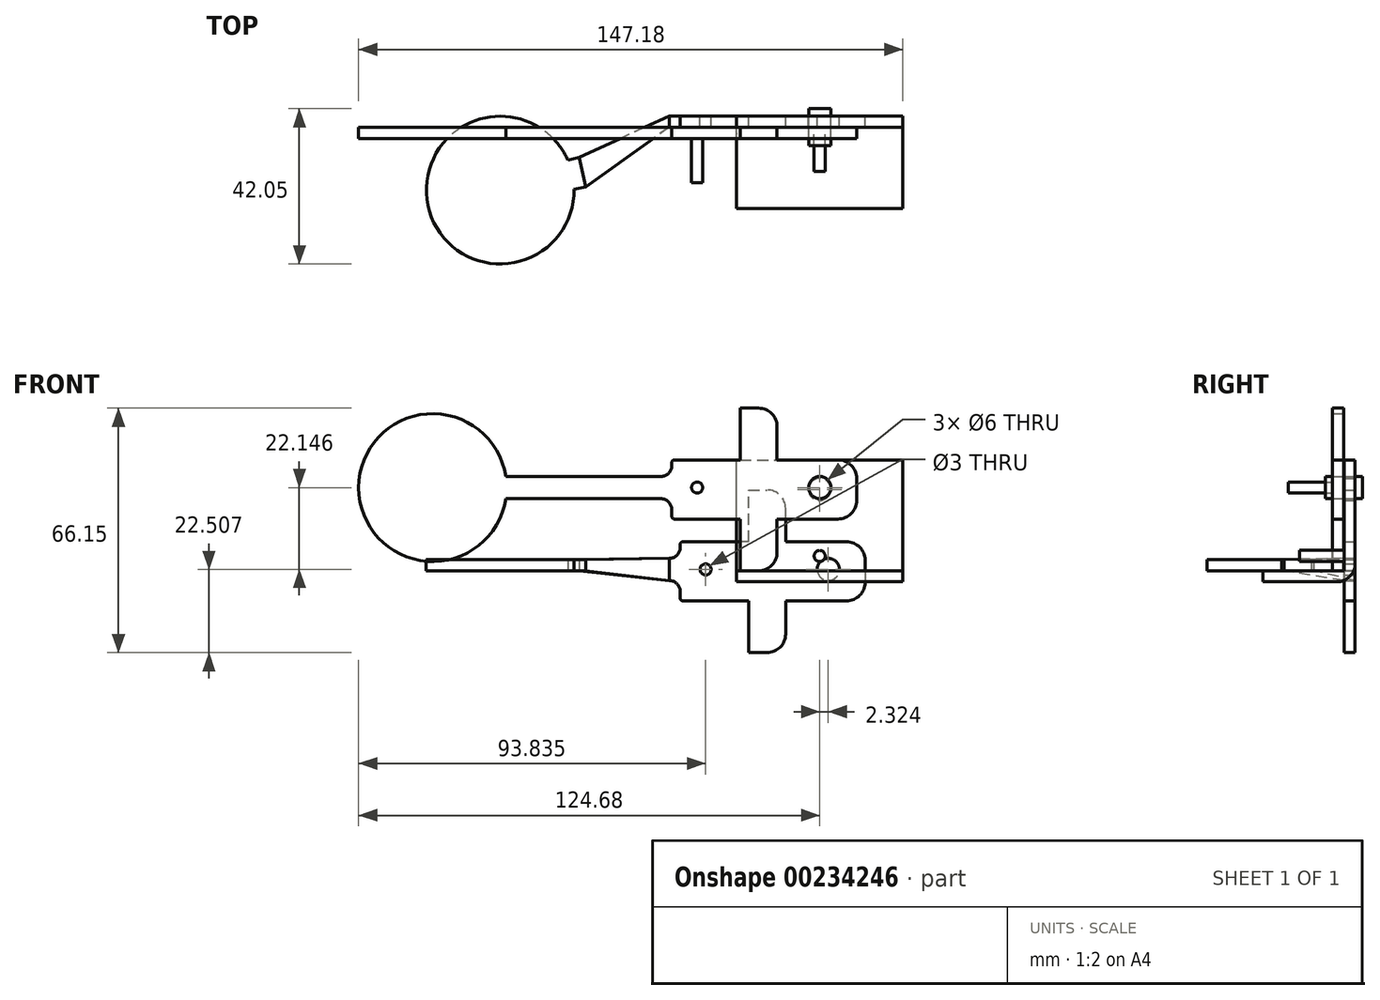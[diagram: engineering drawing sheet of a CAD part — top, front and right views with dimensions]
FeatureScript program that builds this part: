
annotation { "Feature Type Name" : "Feature", "Feature Type Description" : "" }
export const myFeature = defineFeature(function(context is Context, id is Id, definition is map)
    precondition{}
    {
        {
            var Q0;
            Q0=qCreatedBy(makeId("Front.planeOp"),FACE);
            var sketch = newSketch(context, id + "F0", { "sketchPlane" : qUnion([Q0])});
            skLineSegment(sketch, "E0.bottom", {"start": v(0, 0) * mm, "end": v(45, 0) * mm});
            skLineSegment(sketch, "E0.top", {"start": v(0, 30) * mm, "end": v(45, 30) * mm});
            skLineSegment(sketch, "E0.left", {"start": v(0, 0) * mm, "end": v(0, 30) * mm});
            skLineSegment(sketch, "E0.right", {"start": v(45, 0) * mm, "end": v(45, 30) * mm});
            skLineSegment(sketch, "E1.top", {"start": v(0, -3) * mm, "end": v(45, -3) * mm});
            skLineSegment(sketch, "E1.left", {"start": v(0, 0) * mm, "end": v(0, -3) * mm});
            skLineSegment(sketch, "E1.right", {"start": v(45, 0) * mm, "end": v(45, -3) * mm});
            skPoint(sketch, "E2", {"position": v(22.5, 22) * mm});
            skCircle(sketch, "E3", {"center": v(22.5, 4) * mm, "radius": 1.5 * mm});
            skSolve(sketch);
        }
        {
            var Q0;
            Q0=makeQuery(id+"F0.imprint","IMPRINT",FACE,{"disambiguationData":[TD([[makeQuery(id+"F0.imprint","IMPRINT",EDGE,{"derivedFrom":sQuery(id+"F0.wireOp",EDGE,"E0.top")}),-1.0]])]});
            extrude(context, id + "F1", {"entities" : qUnion([Q0]), "depth" : 3 * mm});
        }
        {
            var Q0;
            Q0=makeQuery(id+"F0.imprint","IMPRINT",FACE,{"disambiguationData":[TD([[makeQuery(id+"F0.imprint","IMPRINT",EDGE,{"derivedFrom":sQuery(id+"F0.wireOp",EDGE,"E0.bottom")}),-1.0]])]});
            extrude(context, id + "F2", {"entities" : qUnion([Q0]), "operationType" : NewBodyOperationType.ADD, "depth" : 25 * mm});
        }
        {
            var Q0;
            Q0=sQuery(id+"F0.wireOp",VERTEX,"E2");
            var Q1;
            Q1=makeQuery(id+"F1.opExtrude","SWEPT_BODY",BODY,{"disambiguationData":[OSD([sQuery(id+"F0.wireOp",EDGE,"E0.top"),sQuery(id+"F0.wireOp",EDGE,"E0.left"),sQuery(id+"F0.wireOp",EDGE,"E0.right"),sQuery(id+"F0.wireOp",EDGE,"E0.bottom")])]});
            hole(context, id + "F3", {"style" : HoleStyle.SIMPLE, "endStyle" : HoleEndStyle.THROUGH, "oppositeDirection" : true, "holeDiameter" : 6 * mm, "startFromSketch" : true, "locations" : qUnion([Q0]), "scope" : qUnion([Q1]), "isTappedThrough" : true});
        }
        {
            var Q0;
            Q0=makeQuery(id+"F2.opExtrude","CAP_EDGE",EDGE,{"disambiguationData":[OSD([sQuery(id+"F0.wireOp",EDGE,"E1.top")])],"isStart":true});
            fillet(context, id + "F4", {"entities" : qUnion([Q0]), "radius" : 5 * mm, "tangentPropagation" : true, "allowEdgeOverflow" : false});
        }
        {
            var Q0;
            Q0=qCreatedBy(makeId("Front.planeOp"),FACE);
            var sketch = newSketch(context, id + "F5", { "sketchPlane" : qUnion([Q0])});
            skCircle(sketch, "E4", {"center": v(22.54, 22.5) * mm, "radius": 3 * mm});
            skLineSegment(sketch, "E5.bottom", {"start": v(27.5, 30) * mm, "end": v(11, 30) * mm});
            skLineSegment(sketch, "E5.top", {"start": v(27.5, 14) * mm, "end": v(11, 14) * mm});
            skLineSegment(sketch, "E5.left", {"start": v(32.5, 25) * mm, "end": v(32.5, 19) * mm});
            skLineSegment(sketch, "E5.right", {"start": v(-17.5, 29.27) * mm, "end": v(-17.5, 28.4) * mm});
            skPoint(sketch, "E6.visualSharp", {"position": v(32.5, 30) * mm});
            skArc(sketch, "E6.filletArc", {"start": v(32.5, 25) * mm, "mid": v(31.04, 28.54) * mm, "end": v(27.5, 30) * mm});
            skPoint(sketch, "E7.visualSharp", {"position": v(32.5, 14) * mm});
            skArc(sketch, "E7.filletArc", {"start": v(27.5, 14) * mm, "mid": v(31.04, 15.46) * mm, "end": v(32.5, 19) * mm});
            skArc(sketch, "E8", {"start": v(-62.4, 25.5) * mm, "mid": v(-102.18, 22.5) * mm, "end": v(-62.4, 19.5) * mm});
            skLineSegment(sketch, "E9.bottom", {"start": v(-20.4, 25.5) * mm, "end": v(-62.4, 25.5) * mm});
            skLineSegment(sketch, "E9.top", {"start": v(-20.5, 19.5) * mm, "end": v(-62.4, 19.5) * mm});
            skLineSegment(sketch, "E10.trimOffspring", {"start": v(-17.5, 16.5) * mm, "end": v(-17.5, 14.73) * mm});
            skPoint(sketch, "E11.visualSharp", {"position": v(-17.5, 25.5) * mm});
            skArc(sketch, "E11.filletArc", {"start": v(-20.4, 25.5) * mm, "mid": v(-18.35, 26.35) * mm, "end": v(-17.5, 28.4) * mm});
            skPoint(sketch, "E12.visualSharp", {"position": v(-17.5, 19.5) * mm});
            skArc(sketch, "E12.filletArc", {"start": v(-17.5, 16.5) * mm, "mid": v(-18.38, 18.62) * mm, "end": v(-20.5, 19.5) * mm});
            skPoint(sketch, "E13.visualSharp", {"position": v(-17.5, 14) * mm});
            skArc(sketch, "E13.filletArc", {"start": v(-17.5, 14.73) * mm, "mid": v(-17.29, 14.21) * mm, "end": v(-16.77, 14) * mm});
            skPoint(sketch, "E14.visualSharp", {"position": v(-17.5, 30) * mm});
            skArc(sketch, "E14.filletArc", {"start": v(-16.77, 30) * mm, "mid": v(-17.29, 29.79) * mm, "end": v(-17.5, 29.27) * mm});
            skLineSegment(sketch, "E15.top", {"start": v(1, 0) * mm, "end": v(6, 0) * mm});
            skLineSegment(sketch, "E15.left", {"start": v(1, 14) * mm, "end": v(1, 0) * mm});
            skLineSegment(sketch, "E15.right", {"start": v(11, 14) * mm, "end": v(11, 5) * mm});
            skLineSegment(sketch, "E16.trimOffspring", {"start": v(1, 14) * mm, "end": v(-16.77, 14) * mm});
            skLineSegment(sketch, "E17.top", {"start": v(1, 44) * mm, "end": v(6, 44) * mm});
            skLineSegment(sketch, "E17.left", {"start": v(1, 30) * mm, "end": v(1, 44) * mm});
            skLineSegment(sketch, "E17.right", {"start": v(11, 30) * mm, "end": v(11, 39) * mm});
            skPoint(sketch, "E18.visualSharp", {"position": v(11, 44) * mm});
            skArc(sketch, "E18.filletArc", {"start": v(11, 39) * mm, "mid": v(9.54, 42.54) * mm, "end": v(6, 44) * mm});
            skPoint(sketch, "E19.visualSharp", {"position": v(11, 0) * mm});
            skArc(sketch, "E19.filletArc", {"start": v(6, 0) * mm, "mid": v(9.54, 1.46) * mm, "end": v(11, 5) * mm});
            skLineSegment(sketch, "E20.trimOffspring", {"start": v(1, 30) * mm, "end": v(-16.77, 30) * mm});
            skCircle(sketch, "E21", {"center": v(-10.63, 22.5) * mm, "radius": 1.5 * mm});
            skSolve(sketch);
        }
        {
            var Q0;
            Q0=makeQuery(id+"F5.imprint","IMPRINT",FACE,{"disambiguationData":[TD([[makeQuery(id+"F5.imprint","IMPRINT",EDGE,{"derivedFrom":sQuery(id+"F5.wireOp",EDGE,"E4")}),-1.0]])]});
            extrude(context, id + "F6", {"entities" : qUnion([Q0]), "depth" : 3 * mm});
        }
        {
            var Q0;
            Q0=makeQuery(id+"F5.imprint","IMPRINT",FACE,{"disambiguationData":[TD([[makeQuery(id+"F5.imprint","IMPRINT",EDGE,{"derivedFrom":sQuery(id+"F5.wireOp",EDGE,"E4")}),1.0]])]});
            var Q1;
            Q1=sQuery(id+"F5.wireOp",EDGE,"E4");
            extrude(context, id + "F7", {"entities" : qUnion([Q0]), "surfaceEntities" : qUnion([Q1]), "depth" : 8 * mm, "hasSecondDirection" : true, "secondDirectionOppositeDirection" : true, "secondDirectionDepth" : 2 * mm});
        }
        {
            var Q0;
            Q0=makeQuery(id+"F5.imprint","IMPRINT",FACE,{"disambiguationData":[TD([[makeQuery(id+"F5.imprint","IMPRINT",EDGE,{"derivedFrom":sQuery(id+"F5.wireOp",EDGE,"E21")}),1.0]])]});
            extrude(context, id + "F8", {"entities" : qUnion([Q0]), "operationType" : NewBodyOperationType.ADD, "depth" : 15 * mm});
        }
        {
            var Q0;
            Q0=makeQuery(id+"F6.opExtrude","SWEPT_BODY",BODY,{"disambiguationData":[OSD([sQuery(id+"F5.wireOp",EDGE,"E4"),sQuery(id+"F5.wireOp",EDGE,"E5.bottom"),sQuery(id+"F5.wireOp",EDGE,"E5.top"),sQuery(id+"F5.wireOp",EDGE,"E5.left"),sQuery(id+"F5.wireOp",EDGE,"E5.right"),sQuery(id+"F5.wireOp",EDGE,"E6.filletArc"),sQuery(id+"F5.wireOp",EDGE,"E7.filletArc"),sQuery(id+"F5.wireOp",EDGE,"E8"),sQuery(id+"F5.wireOp",EDGE,"E9.bottom"),sQuery(id+"F5.wireOp",EDGE,"E9.top"),sQuery(id+"F5.wireOp",EDGE,"E10.trimOffspring"),sQuery(id+"F5.wireOp",EDGE,"E11.filletArc"),sQuery(id+"F5.wireOp",EDGE,"E12.filletArc"),sQuery(id+"F5.wireOp",EDGE,"E13.filletArc"),sQuery(id+"F5.wireOp",EDGE,"E14.filletArc"),sQuery(id+"F5.wireOp",EDGE,"E15.top"),sQuery(id+"F5.wireOp",EDGE,"E15.left"),sQuery(id+"F5.wireOp",EDGE,"E15.right"),sQuery(id+"F5.wireOp",EDGE,"E16.trimOffspring"),sQuery(id+"F5.wireOp",EDGE,"E17.top"),sQuery(id+"F5.wireOp",EDGE,"E17.left"),sQuery(id+"F5.wireOp",EDGE,"E17.right"),sQuery(id+"F5.wireOp",EDGE,"E18.filletArc"),sQuery(id+"F5.wireOp",EDGE,"E19.filletArc"),sQuery(id+"F5.wireOp",EDGE,"E20.trimOffspring"),sQuery(id+"F5.wireOp",EDGE,"E21")])]});
            transform(context, id + "F9", {"entities" : qUnion([Q0]), "transformType" : TransformType.TRANSLATION_3D, "dx" : 0 * mm, "dy" : -3.1 * mm, "dz" : 0 * mm, "makeCopy" : false});
        }
        {
            var Q0;
            Q0=makeQuery(id+"F0.imprint","IMPRINT",FACE,{"disambiguationData":[TD([[makeQuery(id+"F0.imprint","IMPRINT",EDGE,{"derivedFrom":sQuery(id+"F0.wireOp",EDGE,"E3")}),1.0]])]});
            extrude(context, id + "F10", {"entities" : qUnion([Q0]), "operationType" : NewBodyOperationType.ADD, "depth" : 15 * mm});
        }
        {
            var Q0;
            Q0=qCreatedBy(makeId("Top.planeOp"),FACE);
            var sketch = newSketch(context, id + "F11", { "sketchPlane" : qUnion([Q0])});
            skArc(sketch, "E22", {"start": v(-45.62, -11.89) * mm, "mid": v(-83.41, -24.34) * mm, "end": v(-43.88, -19.84) * mm});
            skLineSegment(sketch, "E23.bottom", {"start": v(-45.62, -11.89) * mm, "end": v(-42.5, -11.22) * mm});
            skLineSegment(sketch, "E23.top", {"start": v(-43.91, -19.84) * mm, "end": v(-40.8, -19.18) * mm});
            skLineSegment(sketch, "E23.right", {"start": v(-42.5, -11.22) * mm, "end": v(-40.8, -19.18) * mm});
            skSolve(sketch);
        }
        {
            var Q0;
            Q0=qCreatedBy(makeId("Front.planeOp"),FACE);
            var sketch = newSketch(context, id + "F12", { "sketchPlane" : qUnion([Q0])});
            skCircle(sketch, "E24", {"center": v(24.82, 0.36) * mm, "radius": 3 * mm});
            skLineSegment(sketch, "E25.bottom", {"start": v(29.79, 7.85) * mm, "end": v(13.29, 7.85) * mm});
            skLineSegment(sketch, "E25.top", {"start": v(29.79, -8.15) * mm, "end": v(13.29, -8.15) * mm});
            skLineSegment(sketch, "E25.left", {"start": v(34.79, 2.85) * mm, "end": v(34.79, -3.15) * mm});
            skLineSegment(sketch, "E25.right", {"start": v(-15.21, 7.12) * mm, "end": v(-15.21, 6.26) * mm});
            skPoint(sketch, "E26.visualSharp", {"position": v(34.79, 7.85) * mm});
            skArc(sketch, "E26.filletArc", {"start": v(34.79, 2.85) * mm, "mid": v(33.32, 6.4) * mm, "end": v(29.79, 7.85) * mm});
            skPoint(sketch, "E27.visualSharp", {"position": v(34.79, -8.15) * mm});
            skArc(sketch, "E27.filletArc", {"start": v(29.79, -8.15) * mm, "mid": v(33.32, -6.68) * mm, "end": v(34.79, -3.15) * mm});
            skLineSegment(sketch, "E28.trimOffspring", {"start": v(-15.21, -5.64) * mm, "end": v(-15.21, -7.41) * mm});
            skPoint(sketch, "E29.visualSharp", {"position": v(-15.21, 3.36) * mm});
            skArc(sketch, "E29.filletArc", {"start": v(-18.12, 3.36) * mm, "mid": v(-16.06, 4.2) * mm, "end": v(-15.21, 6.26) * mm});
            skPoint(sketch, "E30.visualSharp", {"position": v(-15.21, -2.64) * mm});
            skArc(sketch, "E30.filletArc", {"start": v(-15.21, -5.64) * mm, "mid": v(-16.1, -3.52) * mm, "end": v(-18.21, -2.64) * mm});
            skPoint(sketch, "E31.visualSharp", {"position": v(-15.21, -8.15) * mm});
            skArc(sketch, "E31.filletArc", {"start": v(-15.21, -7.41) * mm, "mid": v(-15, -7.93) * mm, "end": v(-14.48, -8.15) * mm});
            skPoint(sketch, "E32.visualSharp", {"position": v(-15.21, 7.85) * mm});
            skArc(sketch, "E32.filletArc", {"start": v(-14.48, 7.85) * mm, "mid": v(-15, 7.64) * mm, "end": v(-15.21, 7.12) * mm});
            skLineSegment(sketch, "E33.top", {"start": v(3.29, -22.15) * mm, "end": v(8.29, -22.15) * mm});
            skLineSegment(sketch, "E33.left", {"start": v(3.29, -8.15) * mm, "end": v(3.29, -22.15) * mm});
            skLineSegment(sketch, "E33.right", {"start": v(13.29, -8.15) * mm, "end": v(13.29, -17.15) * mm});
            skLineSegment(sketch, "E34.trimOffspring", {"start": v(3.29, -8.15) * mm, "end": v(-14.48, -8.15) * mm});
            skLineSegment(sketch, "E35.top", {"start": v(3.29, 21.85) * mm, "end": v(8.29, 21.85) * mm});
            skLineSegment(sketch, "E35.left", {"start": v(3.29, 7.85) * mm, "end": v(3.29, 21.85) * mm});
            skLineSegment(sketch, "E35.right", {"start": v(13.29, 7.85) * mm, "end": v(13.29, 16.85) * mm});
            skPoint(sketch, "E36.visualSharp", {"position": v(13.29, 21.85) * mm});
            skArc(sketch, "E36.filletArc", {"start": v(13.29, 16.85) * mm, "mid": v(11.82, 20.4) * mm, "end": v(8.29, 21.85) * mm});
            skPoint(sketch, "E37.visualSharp", {"position": v(13.29, -22.15) * mm});
            skArc(sketch, "E37.filletArc", {"start": v(8.29, -22.15) * mm, "mid": v(11.82, -20.68) * mm, "end": v(13.29, -17.15) * mm});
            skLineSegment(sketch, "E38.trimOffspring", {"start": v(3.29, 7.85) * mm, "end": v(-14.48, 7.85) * mm});
            skCircle(sketch, "E39", {"center": v(-8.34, 0.36) * mm, "radius": 1.5 * mm});
            skLineSegment(sketch, "E40", {"start": v(-18.12, 3.36) * mm, "end": v(-18.21, -2.64) * mm});
            skSolve(sketch);
        }
        {
            var Q0;
            {var subQ0=sQuery(id+"F11.wireOp",EDGE,"E22");Q0=makeQuery(id+"F11.imprint","IMPRINT",FACE,{"disambiguationData":[TD([[makeQuery(id+"F11.imprint","IMPRINT",EDGE,{"derivedFrom":subQ0}),1.0]])]});}
            extrude(context, id + "F13", {"entities" : qUnion([Q0]), "depth" : 3 * mm});
        }
        {
            var Q0;
            Q0=makeQuery(id+"F12.imprint","IMPRINT",FACE,{"disambiguationData":[TD([[makeQuery(id+"F12.imprint","IMPRINT",EDGE,{"derivedFrom":sQuery(id+"F12.wireOp",EDGE,"E24")}),-1.0]])]});
            extrude(context, id + "F14", {"entities" : qUnion([Q0]), "depth" : 3 * mm});
        }
        {
            var Q0;
            Q0=makeQuery(id+"F14.opExtrude","SWEPT_FACE",FACE,{"disambiguationData":[OSD([sQuery(id+"F12.wireOp",EDGE,"E40")])]});
            var Q1;
            Q1=makeQuery(id+"F13.opExtrude","SWEPT_FACE",FACE,{"disambiguationData":[OSD([sQuery(id+"F11.wireOp",EDGE,"E23.right")])]});
            loft(context, id + "F15", {"sheetProfilesArray" : [{ "sheetProfileEntities" : qUnion([Q0]) }, { "sheetProfileEntities" : qUnion([Q1]) }]});
        }
    });
